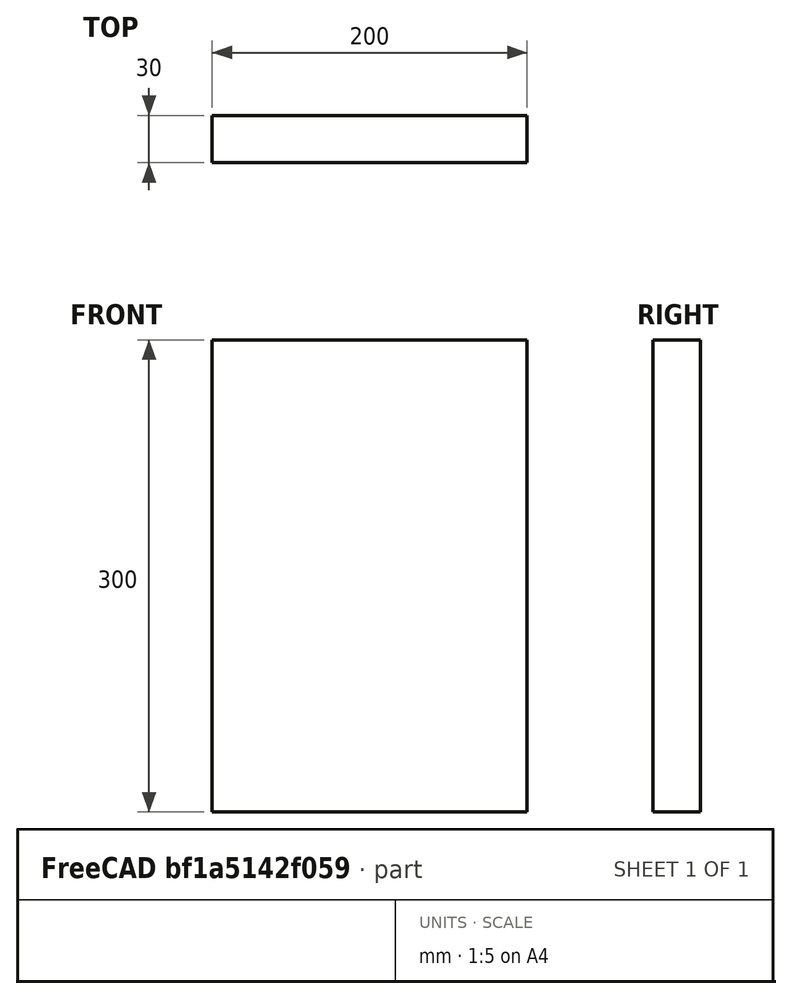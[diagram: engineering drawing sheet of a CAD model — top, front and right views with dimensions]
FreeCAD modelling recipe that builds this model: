
FCSTD DOCUMENT  (FreeCAD 1.0R39319 (Git))
Label: carriage-plate
License: All rights reserved
LicenseURL: https://en.wikipedia.org/wiki/All_rights_reserved
objects: Sketcher::SketchObject×1, PartDesign::Pad×1, PartDesign::Body×1
note: 6 computed .brp shape members not serialized (recipe doc carries the construction recipe); baked Part::Feature solids carry a one-line shape summary decoded from their .brp

FEATURE [Sketcher::SketchObject] Sketch
  ArcFitTolerance = 1e-06
  AttachmentSupport = -> [XZ_Plane]
  FullyConstrained = true
  MakeInternals = false
  MapMode = 5
  Placement = pos=(0,0,0) rot=(1,0,0;1.5708rad)
  sketch-geometry (4):
    g0: LineSegment StartX=0 StartY=0 StartZ=0 EndX=200 EndY=0 EndZ=0
    g1: LineSegment StartX=200 StartY=0 StartZ=0 EndX=200 EndY=300 EndZ=0
    g2: LineSegment StartX=200 StartY=300 StartZ=0 EndX=0 EndY=300 EndZ=0
    g3: LineSegment StartX=0 StartY=300 StartZ=0 EndX=0 EndY=0 EndZ=0
  constraints (11):
    c: Coincident(g0,g1)
    c: Coincident(g1,g2)
    c: Coincident(g2,g3)
    c: Coincident(g3,g0)
    c: Horizontal(g0)
    c: Horizontal(g2)
    c: Vertical(g1)
    c: Vertical(g3)
    c: Distance(g1,g3) = 200
    c: Distance(g0,g2) = 300
    c: Coincident(g0,g-1)
FEATURE [PartDesign::Pad] Pad
  Direction = (0,-1,2e-16)
  Length = 30
  Length2 = 10
  Placement = pos=(0,0,0) rot=(1,0,0;1.5708rad)
  Profile = -> Sketch
  ReferenceAxis = -> Sketch [N_Axis]
  Refine = true
  Suppressed = false
  Type = 0
FEATURE [PartDesign::Body] Body
  AllowCompound = false
  Group = -> [Sketch,Pad]
  Origin = -> Origin
  Tip = -> Pad
